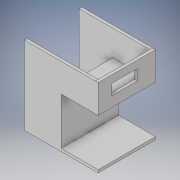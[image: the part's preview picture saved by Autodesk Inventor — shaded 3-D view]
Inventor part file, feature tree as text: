
AUTODESK INVENTOR PART (.ipt)
format: ipt  version: 2018 (Build 220112000, 112)  size: 206,336 bytes
history: native  units: in
note: dims shown in document units (in); Inventor stores cm internally (conversion verified against a paired STEP export)
features: extrude x8, sketch x8, other x1, mirror x1
ambient origin geometry x8: Origin, YZ Plane, XZ Plane, XY Plane, X Axis, Y Axis, Z Axis, Center Point
bodies: Body1 (feature_tree), Body2 (feature_tree), Body3 (feature_tree), Body4 (feature_tree)
feature tree (18):
  other  "Sólido1"
  extrude  "Extrusión1"  Depth=0.508in
  extrude  "Extrusión2"  Depth=1.304in
  mirror  "Simetría1"
  extrude  "Extrusión3"  Depth=0.652in
  extrude  "Extrusión4"  Depth=0.05in TaperAngle=0.0deg
  extrude  "Extrusión7"  Depth=0.05in TaperAngle=0.0deg
  extrude  "Extrusión8"  Depth=0.05in
  extrude  "Extrusión9"  Depth=0.05in
  extrude  "Extrusión10"  Depth=0.1885in
  sketch  "Boceto1"  dims[d0=0.652in d1=0.508in]
  sketch  "Boceto2"  dims[d2=0.05in d3=0.0in d4=1.304in]
  sketch  "Boceto3"  dims[d5=0.5in d6=0.652in]
  sketch  "Boceto4"  dims[d7=0.8343in d8=0.05in d9=0.0in]
  sketch  "Boceto7"  dims[d10=0.8332in d11=0.05in d12=0.0in]
  sketch  "Boceto8"  dims[d14=0.05in d15=0.0in d23=0.702in]
  sketch  "Boceto9"  dims[d26=0.05in d27=0.0in d28=0.05in]
  sketch  "Boceto10"  dims[d29=1.016in d30=0.1885in d31=0.458in d36=0.18in d37=0.7in d40=1.0in d41=0.0in d42=0.1853in d43=0.326in d44=0.1382in d45=1.0in d46=0.0in d47=0.0855in d48=0.4165in d49=0.91in d50=0.1in d51=0.4165in d52=1.0in d53=0.0in]
